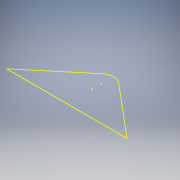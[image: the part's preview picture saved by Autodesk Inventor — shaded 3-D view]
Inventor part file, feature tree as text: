
AUTODESK INVENTOR PART (.ipt)
format: ipt  version: 2016 (Build 200138000, 138)  size: 78,848 bytes
history: native  units: mm
features: sketch x1, reference x1
ambient origin geometry x8: Origin, YZ Plane, XZ Plane, XY Plane, X Axis, Y Axis, Z Axis, Center Point
feature tree (2):
  sketch  "Sketch1"
  reference  "Reference1"
